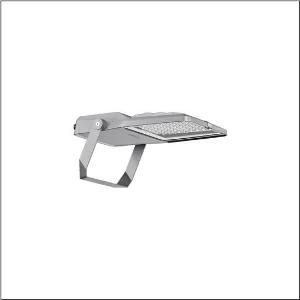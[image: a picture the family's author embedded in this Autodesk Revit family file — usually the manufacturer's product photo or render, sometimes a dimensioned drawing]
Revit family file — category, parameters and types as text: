
# Revit family: floodlight_fl_21_iq_mini___pl61_5xa7772c3c1a_b73e
name_source: partatom
category: Lighting Fixtures
units: mm (PartAtom-declared; Revit-internal decimal feet)

## family parameters
Cut with Voids When Loaded = No
Host = Face
Light Source = No
Part Type = Normal
Room Calculation Point = No
Round Connector Dimension = Use Diameter
Shared = No

## types (1)
- --- (1 x LED, 10320 lm, 87.2 W, 3000K)
    Apparent Load = 87 VA
    CIE Flux Codes = 33 65 98 100 100
    Color Rendering = 80
    Color Temperature = 3000K
    Default Elevation = 1800 mm
    Description = Floodlight FL 21 iQ mini, floodlight, primary light control with lens, of PMMA, primary optical cover: protective disc, of toughened safety glass, transparent, light distribution: PL61, light emission: direct distribution, installation type: surface-mounted, lamps: LED, High Power LED, rated values: 10.320lm | 87,2W | 118,3lm/W (begin service life); end service life: 10.320lm | 92,1W; at 50% lumin. flux: 5.160lm | 40,1W | 128,7lm/W, colour temperature: 3000K, colour rendering: CRI > 80, light colour: 830, light setting 1 begin service life: 100% | 10.320lm | 87,2W | 118,3lm/W | 3.000K, light setting 1 end service life: 92,1W, further light settings possible, control: Street-Remote, Auto-Match, Temp-Guard, Night-Set, Smart-Wire, Desk-Remote (wireless, voltage-free reading and setting of iQ features in the workshop via application-optimized NFC function/RFID function), optimised constant luminous flux control (CLO 2.0), pre-setting: linear dimming characteristic, with terminal, 6-pole, mains connection: 220..240V, AC, 50/60Hz, luminaire housing, of diecast aluminium, powder-coated, SITECO metallic grey (DB 702S), corrosivity category C5 mid according to DIN EN ISO 12944suitable for swimming poolschlorine-resistant, sealing non-destructively replaceable, mounting bracket, of steel, galvanised, powder-coated, SITECO metallic grey (DB 702S), protection rating (complete): IP66, insulation class (complete): insulation class II (safety insulation), certification: CE, ENEC, VDE, protection symbol: D, impact resistance: IK08, permissible operating ambient temperature: -40..+40°C, permissible operating ambient temperature for outdoor applications: -40..+50°C, standard: DIN EN 12944, LABS conformity tested according to VDMA 24364:2018-05, packaging unit: 1 piece

Light Distribution: PL61
    Height = 70 mm
    Lamp = 1 x LED
    Lamp Light Flux = 10320 lm
    Lamp Power = 87.2 W
    Lamp count = 1
    Length = 485 mm
    Luminous efficacy = 118 lm/W
    Manufacturer = Siteco
    ModVariant = No
    Model = 5XA7772C3C1A
    Mounting Place = Pole
    Mounting Type = Pole annexe
    Number of Poles = 1
    OnlyDefault = Yes
    Power Factor = 1
    Product Name = Floodlight FL 21 iQ mini | PL61
    Product group = floodlight | pylon annexe
    ProductGroupID = 6201
    Protection Class = Protection class II
    Protection Degree = IP 66
    RLX_Detail_Level = 1
    RLX_Emergency_Light_Flux = 0 lm
    RLX_Emergency_Type = 0
    RLX_Emergency_Type_DB = No
    RlxData = <blob elided: 96449 chars, md5=f13083ca>
    Socket = socket
    Standby Power = 0 W
    System Light Flux = 10320 lm
    System Power = 87 W
    Type Comments = factory setting: luminous flux: 100 % | dim-lin: 254 | 456 mA
    Type Image = l_1006845.jpg
    URL = http://relux.com
    VarID = @adj_174049
    Voltage = 0 V
    Weight = 0.00 kg
    Width = 337 mm

## geometry (parser evidence)
native form markers: Blend x4, Sweep x14
no freeform markers — native parametric forms only
